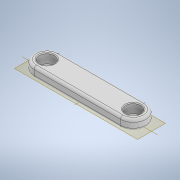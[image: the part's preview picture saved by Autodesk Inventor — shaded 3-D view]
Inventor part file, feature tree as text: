
AUTODESK INVENTOR PART (.ipt)
format: ipt  version: 2020.3 (Build 243373000, 373)  size: 153,600 bytes
history: native  units: mm
features: fillet x2, other x1, extrude x1, sketch x1
ambient origin geometry x8: Origin, YZ Plane, XZ Plane, XY Plane, X Axis, Y Axis, Z Axis, Center Point
bodies: Body1 (feature_tree)
feature tree (5):
  other  "Твердое тело1"
  extrude  "Выдавливание1"  Depth=34.0mm
  fillet  "Сопряжение1"  Radius=10.0mm
  fillet  "Сопряжение2"  Radius=6.0mm
  sketch  "Эскиз1"
